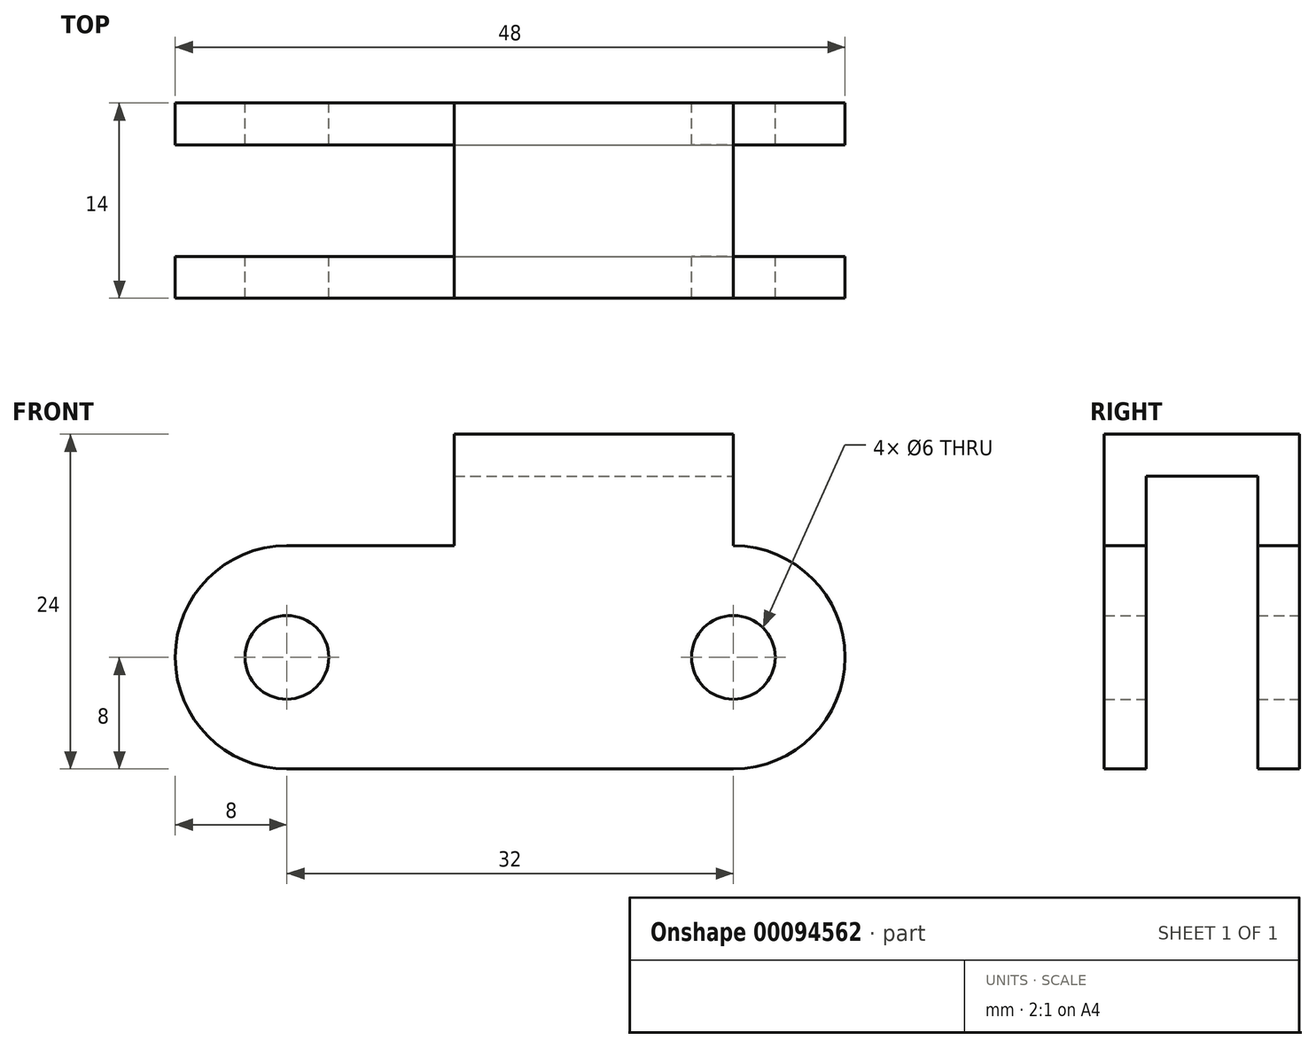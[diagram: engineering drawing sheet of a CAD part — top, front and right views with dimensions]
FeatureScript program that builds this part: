
annotation { "Feature Type Name" : "Feature", "Feature Type Description" : "" }
export const myFeature = defineFeature(function(context is Context, id is Id, definition is map)
    precondition{}
    {
        {
            var Q0;
            Q0=qCreatedBy(makeId("Front.planeOp"),FACE);
            var sketch = newSketch(context, id + "F0", { "sketchPlane" : qUnion([Q0])});
            skLineSegment(sketch, "E0", {"start": v(-32, 0) * mm, "end": v(0, 0) * mm, "construction": true});
            skArc(sketch, "E1.0.startCap", {"start": v(-32, -8) * mm, "mid": v(-40, 0) * mm, "end": v(-32, 8) * mm});
            skArc(sketch, "E1.0.endCap", {"start": v(0, 8) * mm, "mid": v(8, 0) * mm, "end": v(0, -8) * mm});
            skLineSegment(sketch, "E1.0.left", {"start": v(-32, 8) * mm, "end": v(0, 8) * mm});
            skLineSegment(sketch, "E1.0.right", {"start": v(-32, -8) * mm, "end": v(0, -8) * mm});
            skCircle(sketch, "E2", {"center": v(-32, 0) * mm, "radius": 3 * mm});
            skCircle(sketch, "E3.1.0.0", {"center": v(0, 0) * mm, "radius": 3 * mm});
            skLineSegment(sketch, "E4", {"start": v(0, 8) * mm, "end": v(0, 16) * mm});
            skLineSegment(sketch, "E5", {"start": v(0, 16) * mm, "end": v(-20, 16) * mm});
            skLineSegment(sketch, "E6", {"start": v(-20, 16) * mm, "end": v(-20, 8) * mm});
            skSolve(sketch);
        }
        {
            var Q0;
            Q0 = qSketchRegion(id + "F0", true);
            extrude(context, id + "F1", {"entities" : qUnion([Q0]), "endBound" : BoundingType.SYMMETRIC, "depth" : 14 * mm});
        }
        {
            var Q0;
            Q0=qCreatedBy(makeId("Right.planeOp"),FACE);
            var sketch = newSketch(context, id + "F2", { "sketchPlane" : qUnion([Q0])});
            skLineSegment(sketch, "E7.bottom", {"start": v(-4, 13) * mm, "end": v(4, 13) * mm});
            skLineSegment(sketch, "E7.top", {"start": v(-4, -13) * mm, "end": v(4, -13) * mm});
            skLineSegment(sketch, "E7.left", {"start": v(-4, 13) * mm, "end": v(-4, -13) * mm});
            skLineSegment(sketch, "E7.right", {"start": v(4, 13) * mm, "end": v(4, -13) * mm});
            skPoint(sketch, "E7.middle", {"position": v(0, 0) * mm});
            skSolve(sketch);
        }
        {
            var Q0;
            Q0 = qSketchRegion(id + "F2", true);
            extrude(context, id + "F3", {"entities" : qUnion([Q0]), "operationType" : NewBodyOperationType.REMOVE, "endBound" : BoundingType.SYMMETRIC, "oppositeDirection" : true, "depth" : 94.4 * mm});
        }
    });
